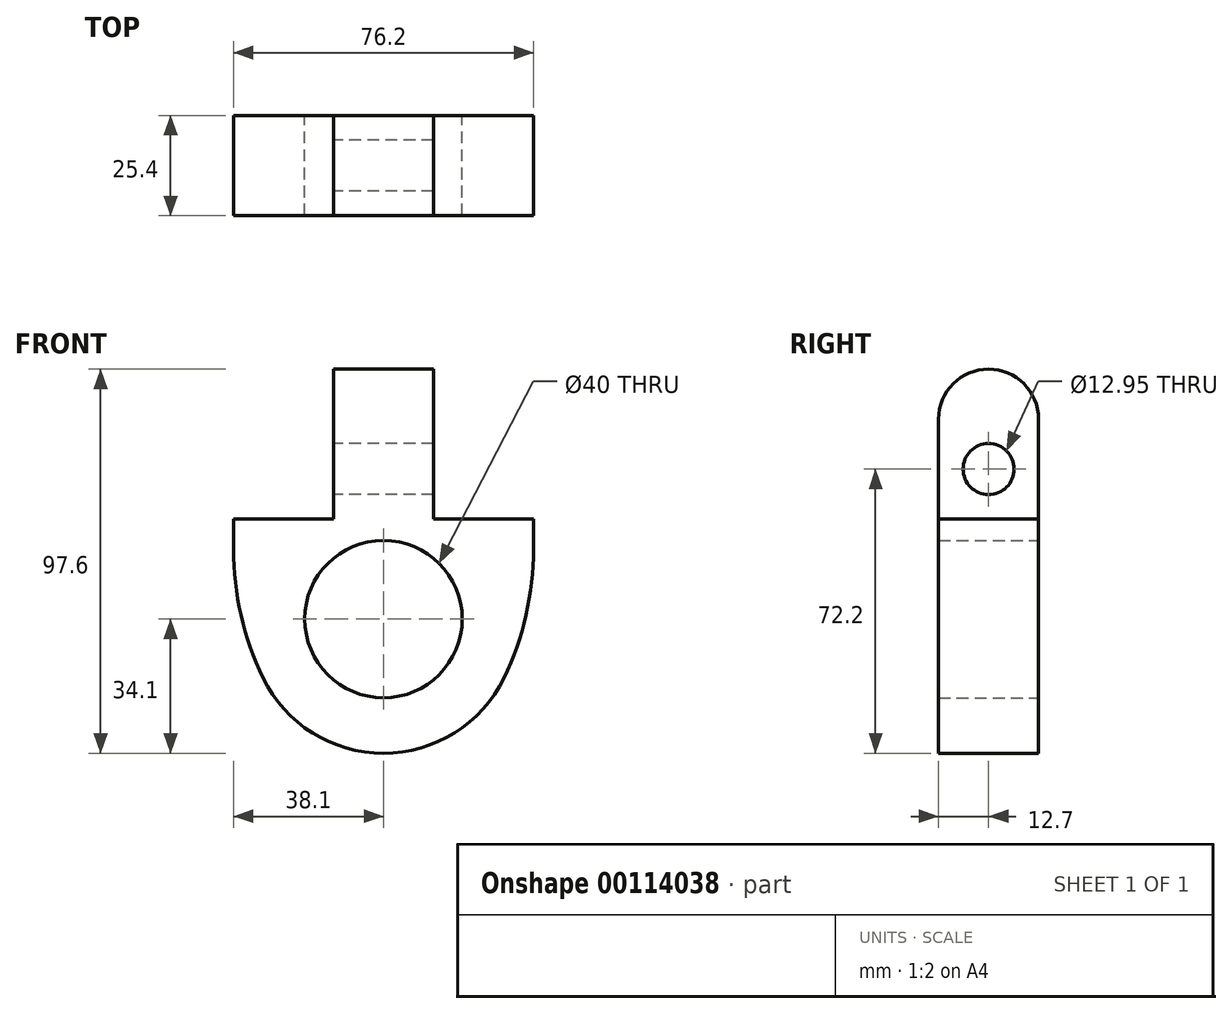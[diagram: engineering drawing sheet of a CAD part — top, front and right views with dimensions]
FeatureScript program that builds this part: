
annotation { "Feature Type Name" : "Feature", "Feature Type Description" : "" }
export const myFeature = defineFeature(function(context is Context, id is Id, definition is map)
    precondition{}
    {
        {
            var Q0;
            Q0=qCreatedBy(makeId("Front.planeOp"),FACE);
            var sketch = newSketch(context, id + "F0", { "sketchPlane" : qUnion([Q0])});
            skCircle(sketch, "E0", {"center": v(0, 0) * mm, "radius": 20 * mm});
            skArc(sketch, "E1", {"start": v(-30.64, -14.96) * mm, "mid": v(0, -34.1) * mm, "end": v(30.64, -14.96) * mm});
            skLineSegment(sketch, "E2", {"start": v(-38.1, 17.78) * mm, "end": v(-38.1, 25.4) * mm});
            skLineSegment(sketch, "E3", {"start": v(38.1, 17.78) * mm, "end": v(38.1, 25.4) * mm});
            skLineSegment(sketch, "E4", {"start": v(-38.1, 25.4) * mm, "end": v(-12.7, 25.4) * mm});
            skLineSegment(sketch, "E5.top", {"start": v(-12.7, 50.8) * mm, "end": v(12.7, 50.8) * mm});
            skLineSegment(sketch, "E5.left", {"start": v(-12.7, 25.4) * mm, "end": v(-12.7, 50.8) * mm});
            skLineSegment(sketch, "E5.right", {"start": v(12.7, 25.4) * mm, "end": v(12.7, 50.8) * mm});
            skLineSegment(sketch, "E6.trimOffspring", {"start": v(12.7, 25.4) * mm, "end": v(38.1, 25.4) * mm});
            skArc(sketch, "E7", {"start": v(-38.1, 17.78) * mm, "mid": v(-36.21, 0.99) * mm, "end": v(-30.64, -14.96) * mm});
            skArc(sketch, "E8", {"start": v(30.64, -14.96) * mm, "mid": v(36.21, 0.99) * mm, "end": v(38.1, 17.78) * mm});
            skSolve(sketch);
        }
        {
            var Q0;
            Q0 = qSketchRegion(id + "F0", true);
            extrude(context, id + "F1", {"entities" : qUnion([Q0]), "endBound" : BoundingType.SYMMETRIC, "depth" : 25.4 * mm});
        }
        {
            var Q0;
            Q0=makeQuery(id+"F1.opExtrude","SWEPT_FACE",FACE,{"disambiguationData":[OSD([sQuery(id+"F0.wireOp",EDGE,"E5.left")])]});
            var sketch = newSketch(context, id + "F2", { "sketchPlane" : qUnion([Q0])});
            skCircle(sketch, "E9", {"center": v(0, 38.1) * mm, "radius": 6.48 * mm});
            skPoint(sketch, "E10.center.orphan", {"position": v(0, 50.8) * mm});
            skArc(sketch, "E11", {"start": v(12.7, 50.8) * mm, "mid": v(0, 63.5) * mm, "end": v(-12.7, 50.8) * mm});
            skLineSegment(sketch, "E12", {"start": v(-12.7, 50.8) * mm, "end": v(12.7, 50.8) * mm});
            skSolve(sketch);
        }
        {
            var Q0;
            Q0=makeQuery(id+"F2.imprint","IMPRINT",FACE,{"disambiguationData":[TD([[makeQuery(id+"F2.imprint","IMPRINT",EDGE,{"derivedFrom":sQuery(id+"F2.wireOp",EDGE,"E9")}),1.0]])]});
            extrude(context, id + "F3", {"entities" : qUnion([Q0]), "operationType" : NewBodyOperationType.REMOVE, "endBound" : BoundingType.THROUGH_ALL, "oppositeDirection" : true, "depth" : 25.4 * mm});
        }
        {
            var Q0;
            Q0=makeQuery(id+"F2.imprint","IMPRINT",FACE,{"disambiguationData":[TD([[makeQuery(id+"F2.imprint","IMPRINT",EDGE,{"derivedFrom":sQuery(id+"F2.wireOp",EDGE,"E11")}),1.0]])]});
            extrude(context, id + "F4", {"entities" : qUnion([Q0]), "operationType" : NewBodyOperationType.ADD, "oppositeDirection" : true, "depth" : 25.4 * mm});
        }
    });
